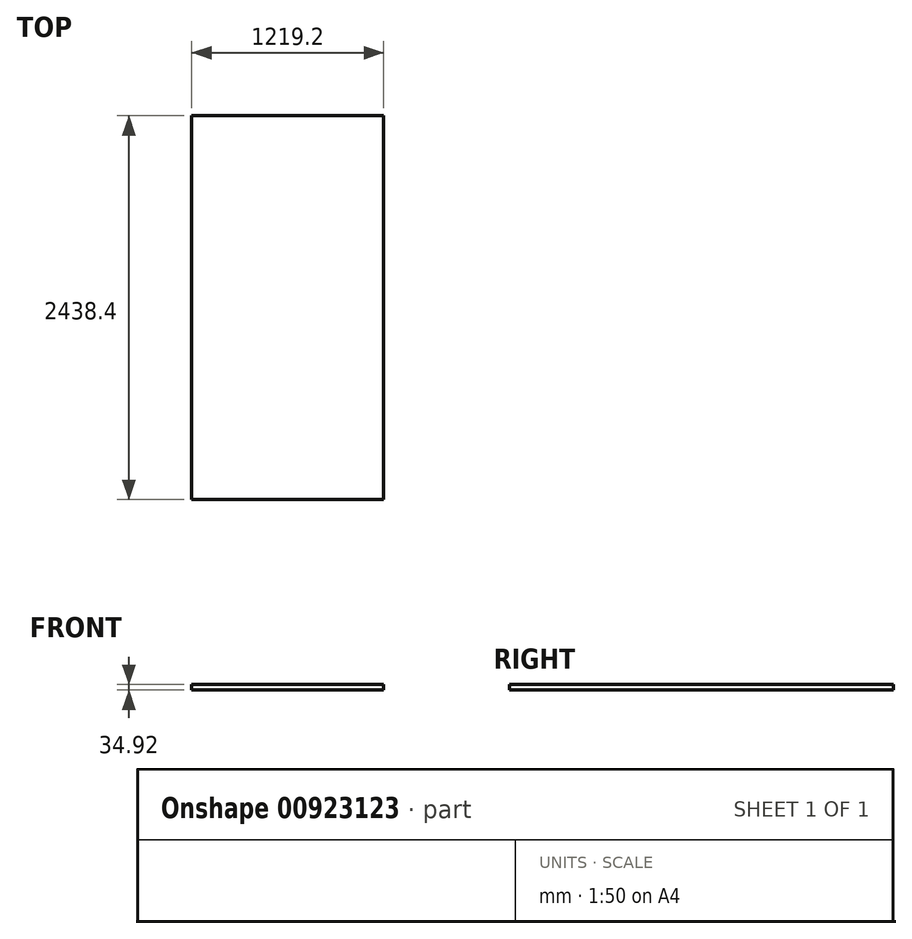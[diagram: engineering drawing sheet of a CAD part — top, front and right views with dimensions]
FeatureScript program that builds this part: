
annotation { "Feature Type Name" : "Feature", "Feature Type Description" : "" }
export const myFeature = defineFeature(function(context is Context, id is Id, definition is map)
    precondition{}
    {
        {
            var Q0;
            Q0=qCreatedBy(makeId("Top.planeOp"),FACE);
            var sketch = newSketch(context, id + "F0", { "sketchPlane" : qUnion([Q0])});
            skLineSegment(sketch, "E0.bottom", {"start": v(609.6, 1219.2) * mm, "end": v(-609.6, 1219.2) * mm});
            skLineSegment(sketch, "E0.top", {"start": v(609.6, -1219.2) * mm, "end": v(-609.6, -1219.2) * mm});
            skLineSegment(sketch, "E0.left", {"start": v(609.6, 1219.2) * mm, "end": v(609.6, -1219.2) * mm});
            skLineSegment(sketch, "E0.right", {"start": v(-609.6, 1219.2) * mm, "end": v(-609.6, -1219.2) * mm});
            skPoint(sketch, "E0.middle", {"position": v(0, 0) * mm});
            skSolve(sketch);
        }
        {
            var Q0;
            Q0 = qSketchRegion(id + "F0", true);
            extrude(context, id + "F1", {"entities" : qUnion([Q0]), "depth" : 34.92 * mm, "offsetDistance" : 25.4 * mm});
        }
    });
